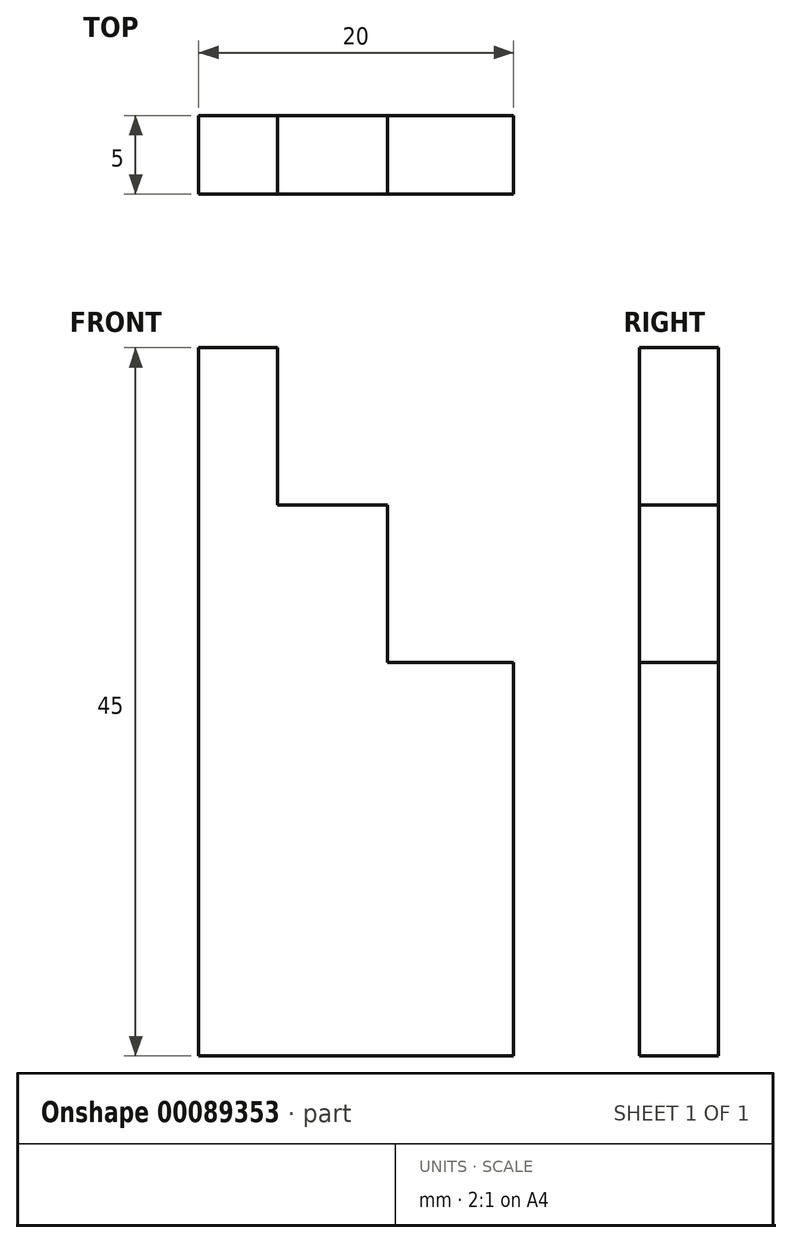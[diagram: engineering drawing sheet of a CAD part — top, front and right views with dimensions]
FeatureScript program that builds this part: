
annotation { "Feature Type Name" : "Feature", "Feature Type Description" : "" }
export const myFeature = defineFeature(function(context is Context, id is Id, definition is map)
    precondition{}
    {
        {
            var Q0;
            Q0=qCreatedBy(makeId("Front.planeOp"),FACE);
            var sketch = newSketch(context, id + "F0", { "sketchPlane" : qUnion([Q0])});
            skLineSegment(sketch, "E0", {"start": v(0, 0) * mm, "end": v(0, 45) * mm});
            skLineSegment(sketch, "E1", {"start": v(0, 45) * mm, "end": v(5, 45) * mm});
            skLineSegment(sketch, "E2", {"start": v(5, 45) * mm, "end": v(5, 35) * mm});
            skLineSegment(sketch, "E3", {"start": v(5, 35) * mm, "end": v(12, 35) * mm});
            skLineSegment(sketch, "E4", {"start": v(12, 35) * mm, "end": v(12, 25) * mm});
            skLineSegment(sketch, "E5", {"start": v(12, 25) * mm, "end": v(20, 25) * mm});
            skLineSegment(sketch, "E6", {"start": v(20, 25) * mm, "end": v(20, 0) * mm});
            skLineSegment(sketch, "E7", {"start": v(20, 0) * mm, "end": v(0, 0) * mm});
            skSolve(sketch);
        }
        {
            var Q0;
            Q0 = qSketchRegion(id + "F0", true);
            extrude(context, id + "F1", {"entities" : qUnion([Q0]), "depth" : 5 * mm});
        }
    });
